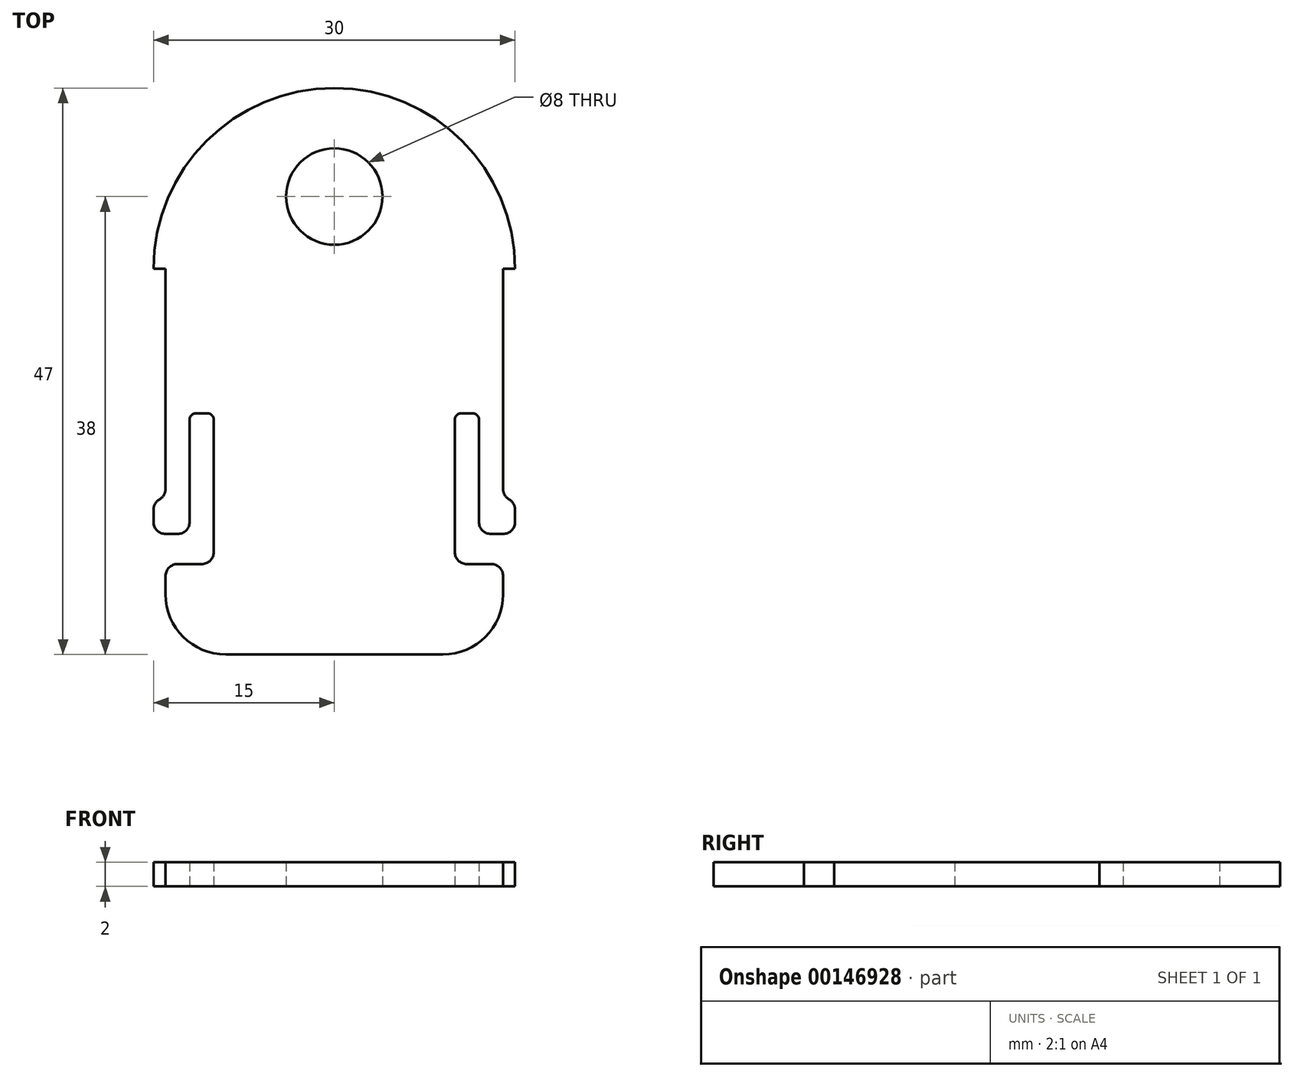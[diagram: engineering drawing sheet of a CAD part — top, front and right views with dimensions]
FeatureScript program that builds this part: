
annotation { "Feature Type Name" : "Feature", "Feature Type Description" : "" }
export const myFeature = defineFeature(function(context is Context, id is Id, definition is map)
    precondition{}
    {
        {
            var Q0;
            Q0=qCreatedBy(makeId("Top.planeOp"),FACE);
            var sketch = newSketch(context, id + "F0", { "sketchPlane" : qUnion([Q0])});
            skLineSegment(sketch, "E0.bottom", {"start": v(-9, 0) * mm, "end": v(9, 0) * mm});
            skPoint(sketch, "E0.middle", {"position": v(0, 0) * mm});
            skArc(sketch, "E1.filletArc", {"start": v(-14, 5) * mm, "mid": v(-12.54, 1.46) * mm, "end": v(-9, 0) * mm});
            skArc(sketch, "E2.filletArc", {"start": v(9, 0) * mm, "mid": v(12.54, 1.46) * mm, "end": v(14, 5) * mm});
            skArc(sketch, "E3", {"start": v(15, 32) * mm, "mid": v(0, 47) * mm, "end": v(-15, 32) * mm});
            skLineSegment(sketch, "E4", {"start": v(-14, 32) * mm, "end": v(-15, 32) * mm});
            skLineSegment(sketch, "E5", {"start": v(14, 32) * mm, "end": v(15, 32) * mm});
            skLineSegment(sketch, "E6", {"start": v(-13, 7.5) * mm, "end": v(-11, 7.5) * mm});
            skLineSegment(sketch, "E7", {"start": v(-10, 8.5) * mm, "end": v(-10, 19.5) * mm});
            skLineSegment(sketch, "E8", {"start": v(-10.5, 20) * mm, "end": v(-11.5, 20) * mm});
            skLineSegment(sketch, "E9", {"start": v(-12, 19.5) * mm, "end": v(-12, 11) * mm});
            skLineSegment(sketch, "E10", {"start": v(-13, 10) * mm, "end": v(-14, 10) * mm});
            skLineSegment(sketch, "E11", {"start": v(-15, 11) * mm, "end": v(-15, 12) * mm});
            skLineSegment(sketch, "E12", {"start": v(-14, 13) * mm, "end": v(-14, 13) * mm});
            skLineSegment(sketch, "E13", {"start": v(-14, 13.73) * mm, "end": v(-14, 32) * mm});
            skLineSegment(sketch, "E14", {"start": v(-14, 6.5) * mm, "end": v(-14, 5) * mm});
            skPoint(sketch, "E15.visualSharp", {"position": v(-10, 20) * mm});
            skArc(sketch, "E15.filletArc", {"start": v(-10, 19.5) * mm, "mid": v(-10.15, 19.85) * mm, "end": v(-10.5, 20) * mm});
            skPoint(sketch, "E16.visualSharp", {"position": v(-12, 20) * mm});
            skArc(sketch, "E16.filletArc", {"start": v(-11.5, 20) * mm, "mid": v(-11.85, 19.85) * mm, "end": v(-12, 19.5) * mm});
            skPoint(sketch, "E17.visualSharp", {"position": v(-12, 10) * mm});
            skArc(sketch, "E17.filletArc", {"start": v(-13, 10) * mm, "mid": v(-12.3, 10.3) * mm, "end": v(-12, 11) * mm});
            skPoint(sketch, "E18.visualSharp", {"position": v(-15, 10) * mm});
            skArc(sketch, "E18.filletArc", {"start": v(-15, 11) * mm, "mid": v(-14.7, 10.3) * mm, "end": v(-14, 10) * mm});
            skPoint(sketch, "E19.visualSharp", {"position": v(-10, 7.5) * mm});
            skArc(sketch, "E19.filletArc", {"start": v(-11, 7.5) * mm, "mid": v(-10.3, 7.8) * mm, "end": v(-10, 8.5) * mm});
            skPoint(sketch, "E20.visualSharp", {"position": v(-14, 7.5) * mm});
            skArc(sketch, "E20.filletArc", {"start": v(-13, 7.5) * mm, "mid": v(-13.7, 7.2) * mm, "end": v(-14, 6.5) * mm});
            skPoint(sketch, "E21.visualSharp", {"position": v(-15, 13) * mm});
            skArc(sketch, "E21.filletArc", {"start": v(-14.5, 12.87) * mm, "mid": v(-14.87, 12.5) * mm, "end": v(-15, 12) * mm});
            skPoint(sketch, "E22.visualSharp", {"position": v(-14, 13) * mm});
            skArc(sketch, "E22.filletArc", {"start": v(-14.5, 12.87) * mm, "mid": v(-14.13, 13.23) * mm, "end": v(-14, 13.73) * mm});
            skCircle(sketch, "E23", {"center": v(0, 38) * mm, "radius": 4 * mm});
            skLineSegment(sketch, "E24", {"start": v(-14, 5) * mm, "end": v(14, 5) * mm, "construction": true});
            skLineSegment(sketch, "E25.MirrorCS", {"start": v(14, 6.5) * mm, "end": v(14, 5) * mm});
            skArc(sketch, "E26.MirrorCS", {"start": v(13, 7.5) * mm, "mid": v(13.7, 7.2) * mm, "end": v(14, 6.5) * mm});
            skLineSegment(sketch, "E27.MirrorCS", {"start": v(13, 7.5) * mm, "end": v(11, 7.5) * mm});
            skArc(sketch, "E28.MirrorCS", {"start": v(11, 7.5) * mm, "mid": v(10.3, 7.8) * mm, "end": v(10, 8.5) * mm});
            skLineSegment(sketch, "E29.MirrorCS", {"start": v(10, 8.5) * mm, "end": v(10, 19.5) * mm});
            skArc(sketch, "E30.MirrorCS", {"start": v(10, 19.5) * mm, "mid": v(10.15, 19.85) * mm, "end": v(10.5, 20) * mm});
            skLineSegment(sketch, "E31.MirrorCS", {"start": v(10.5, 20) * mm, "end": v(11.5, 20) * mm});
            skArc(sketch, "E32.MirrorCS", {"start": v(11.5, 20) * mm, "mid": v(11.85, 19.85) * mm, "end": v(12, 19.5) * mm});
            skLineSegment(sketch, "E33.MirrorCS", {"start": v(12, 19.5) * mm, "end": v(12, 11) * mm});
            skArc(sketch, "E34.MirrorCS", {"start": v(13, 10) * mm, "mid": v(12.3, 10.3) * mm, "end": v(12, 11) * mm});
            skLineSegment(sketch, "E35.MirrorCS", {"start": v(13, 10) * mm, "end": v(14, 10) * mm});
            skArc(sketch, "E36.MirrorCS", {"start": v(15, 11) * mm, "mid": v(14.7, 10.3) * mm, "end": v(14, 10) * mm});
            skLineSegment(sketch, "E37.MirrorCS", {"start": v(15, 11) * mm, "end": v(15, 12) * mm});
            skArc(sketch, "E38.MirrorCS", {"start": v(14.5, 12.87) * mm, "mid": v(14.87, 12.5) * mm, "end": v(15, 12) * mm});
            skArc(sketch, "E39.MirrorCS", {"start": v(14.5, 12.87) * mm, "mid": v(14.13, 13.23) * mm, "end": v(14, 13.73) * mm});
            skLineSegment(sketch, "E40.MirrorCS", {"start": v(14, 13.73) * mm, "end": v(14, 32) * mm});
            skSolve(sketch);
        }
        {
            var Q0;
            Q0 = qSketchRegion(id + "F0", true);
            extrude(context, id + "F1", {"entities" : qUnion([Q0]), "depth" : 2 * mm});
        }
    });
